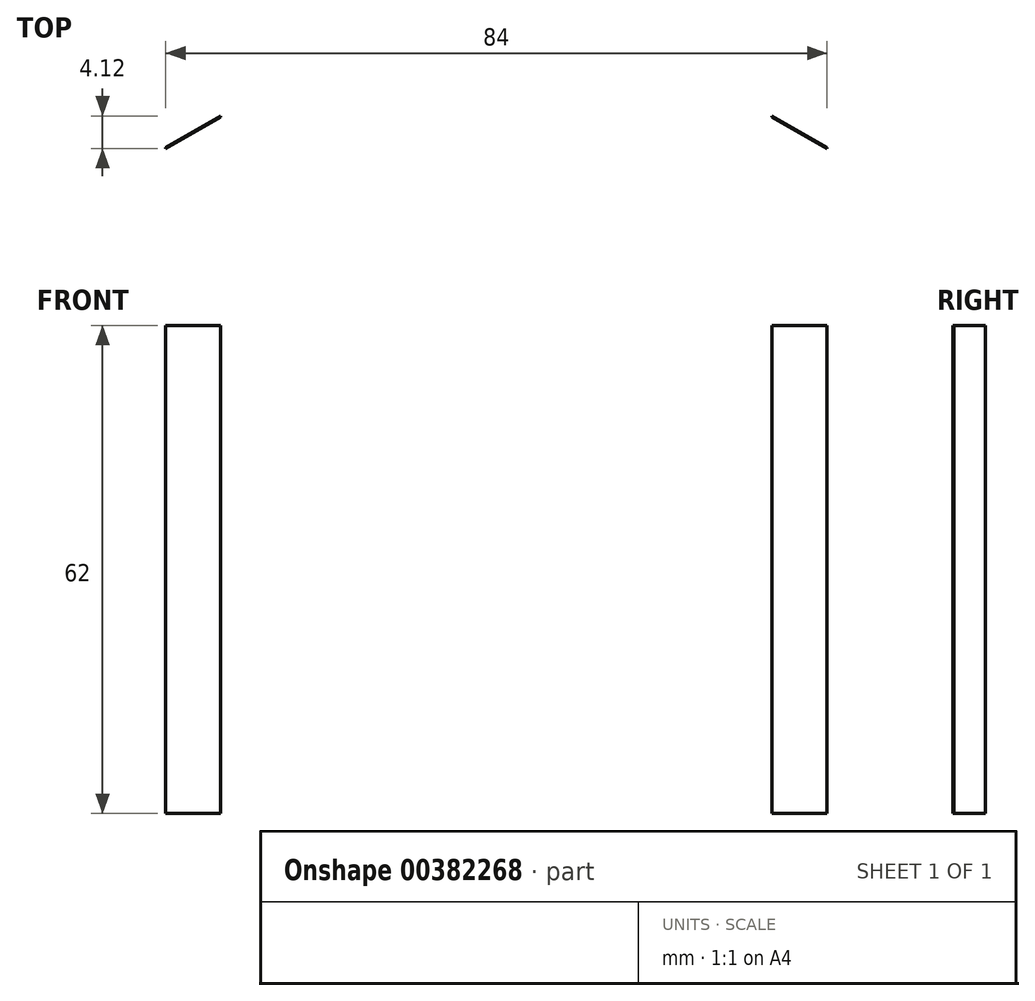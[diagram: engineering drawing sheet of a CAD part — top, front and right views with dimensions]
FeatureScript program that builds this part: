
annotation { "Feature Type Name" : "Feature", "Feature Type Description" : "" }
export const myFeature = defineFeature(function(context is Context, id is Id, definition is map)
    precondition{}
    {
        {
            var Q0;
            Q0=qCreatedBy(makeId("Top.planeOp"),FACE);
            var sketch = newSketch(context, id + "F0", { "sketchPlane" : qUnion([Q0])});
            skPoint(sketch, "E0", {"position": v(0, 0) * mm});
            skPoint(sketch, "E1", {"position": v(35, 0) * mm});
            skPoint(sketch, "E2", {"position": v(-35, 0) * mm});
            skPoint(sketch, "E3", {"position": v(42, 0) * mm});
            skPoint(sketch, "E4", {"position": v(42, -4) * mm});
            skLineSegment(sketch, "E5", {"start": v(0, 34.75) * mm, "end": v(0, -40.78) * mm});
            skLineSegment(sketch, "E6", {"start": v(35, 0) * mm, "end": v(42, -4) * mm});
            skPoint(sketch, "E7", {"position": v(35, -0.12) * mm});
            skLineSegment(sketch, "E8", {"start": v(35, -0.12) * mm, "end": v(42, -4.12) * mm});
            skLineSegment(sketch, "E9", {"start": v(35, 0) * mm, "end": v(35, -0.12) * mm});
            skLineSegment(sketch, "E10", {"start": v(42, -4) * mm, "end": v(42, -4.12) * mm});
            skLineSegment(sketch, "E11.MirrorCS", {"start": v(-35, 0) * mm, "end": v(-42, -4) * mm});
            skLineSegment(sketch, "E12.MirrorCS", {"start": v(-35, -0.12) * mm, "end": v(-42, -4.12) * mm});
            skLineSegment(sketch, "E13.MirrorCS", {"start": v(-42, -4) * mm, "end": v(-42, -4.12) * mm});
            skLineSegment(sketch, "E14.MirrorCS", {"start": v(-35, 0) * mm, "end": v(-35, -0.12) * mm});
            skSolve(sketch);
        }
        {
            var Q0;
            Q0=makeQuery(id+"F0.imprint","IMPRINT",FACE,{"disambiguationData":[TD([[makeQuery(id+"F0.imprint","IMPRINT",EDGE,{"derivedFrom":sQuery(id+"F0.wireOp",EDGE,"E6")}),-1.0]])]});
            var Q1;
            Q1=makeQuery(id+"F0.imprint","IMPRINT",FACE,{"disambiguationData":[TD([[makeQuery(id+"F0.imprint","IMPRINT",EDGE,{"derivedFrom":sQuery(id+"F0.wireOp",EDGE,"E11.MirrorCS")}),1.0]])]});
            extrude(context, id + "F1", {"entities" : qUnion([Q0, Q1]), "depth" : 62 * mm});
        }
    });
